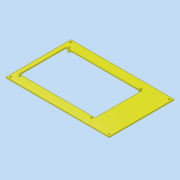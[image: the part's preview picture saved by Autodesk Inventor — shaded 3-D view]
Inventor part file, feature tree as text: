
AUTODESK INVENTOR PART (.ipt)
format: ipt  version: 2022 (Build 260153000, 153)  size: 146,432 bytes
history: native  units: in
note: dims shown in document units (in); Inventor stores cm internally (conversion verified against a paired STEP export)
features: extrude x3, sketch x1
ambient origin geometry x8: Origin, YZ Plane, XZ Plane, XY Plane, X Axis, Y Axis, Z Axis, Center Point
bodies: Solid1 (feature_tree)
feature tree (4):
  extrude  "Extrusion1"  Depth=6.5157in
  extrude  "Extrusion2"  Depth=0.7874in
  extrude  "Extrusion3"  Depth=0.1969in
  sketch  "Sketch3"  dims[d0=3.9961in d1=6.5157in d3=0.7874in d4=0.1378in d5=0.1969in d6=0.1969in d7=0.0787in d8=0.0in d9=0.1378in d11=4.2608in d12=0.0787in d13=0.0in d14=8.878in d16=0.3543in d17=6.19in d18=0.2362in d19=0.2756in d20=0.0in d21=0.1969in d22=0.1969in]
